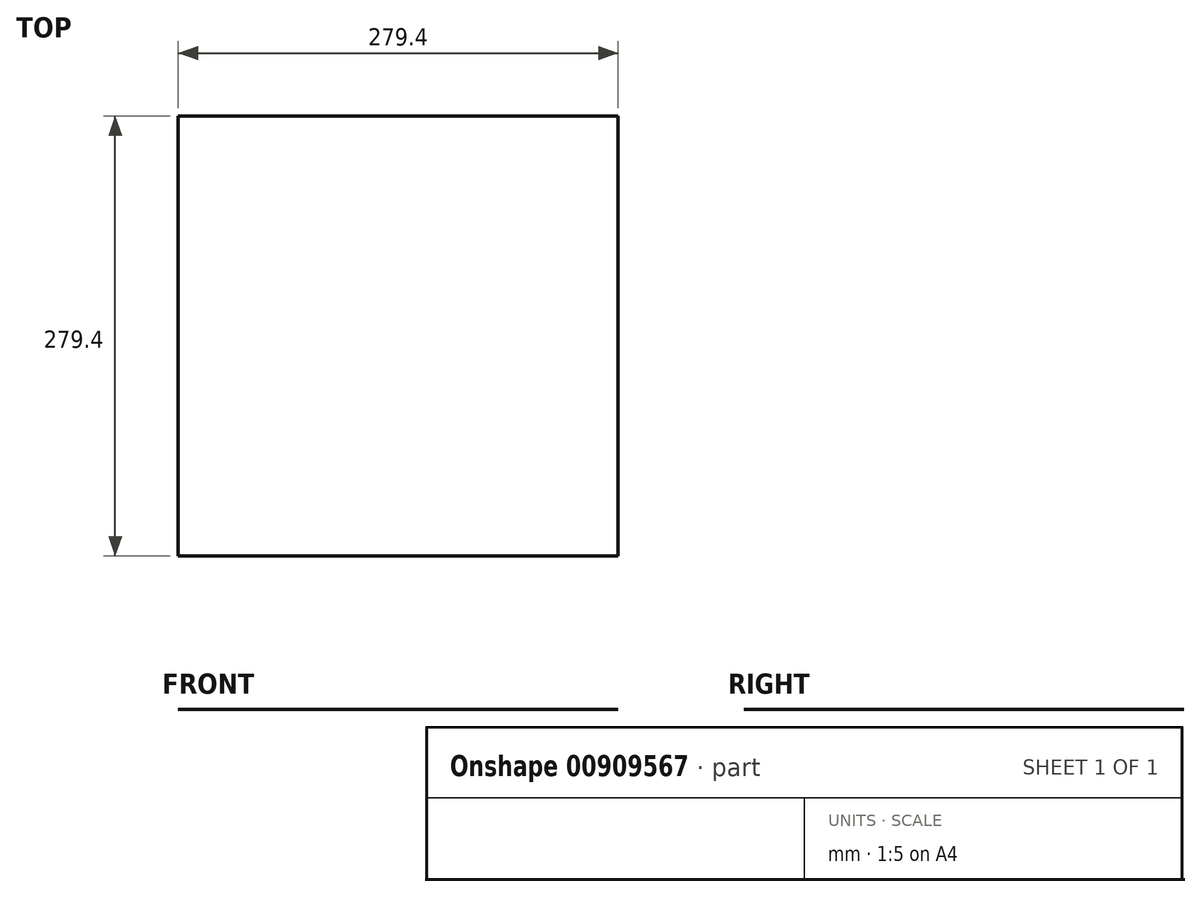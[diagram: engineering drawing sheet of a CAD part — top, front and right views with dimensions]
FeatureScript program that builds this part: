
annotation { "Feature Type Name" : "Feature", "Feature Type Description" : "" }
export const myFeature = defineFeature(function(context is Context, id is Id, definition is map)
    precondition{}
    {
        {
            var Q0;
            Q0=qCreatedBy(makeId("Top.planeOp"),FACE);
            var sketch = newSketch(context, id + "F0", { "sketchPlane" : qUnion([Q0])});
            skLineSegment(sketch, "E0.bottom", {"start": v(-146.95, 170.91) * mm, "end": v(132.45, 170.91) * mm});
            skLineSegment(sketch, "E0.top", {"start": v(-146.95, -108.49) * mm, "end": v(132.45, -108.49) * mm});
            skLineSegment(sketch, "E0.left", {"start": v(-146.95, 170.91) * mm, "end": v(-146.95, -108.49) * mm});
            skLineSegment(sketch, "E0.right", {"start": v(132.45, 170.91) * mm, "end": v(132.45, -108.49) * mm});
            skSolve(sketch);
        }
        {
            var Q0;
            Q0=makeQuery(id+"F0.imprint","IMPRINT",FACE,{"disambiguationData":[TD([[makeQuery(id+"F0.imprint","IMPRINT",EDGE,{"derivedFrom":sQuery(id+"F0.wireOp",EDGE,"E0.bottom")}),-1.0]])]});
            extrude(context, id + "F1", {"entities" : qUnion([Q0]), "depth" : 1 / 406.4 * mm, "offsetDistance" : 25.4 * mm});
        }
    });
